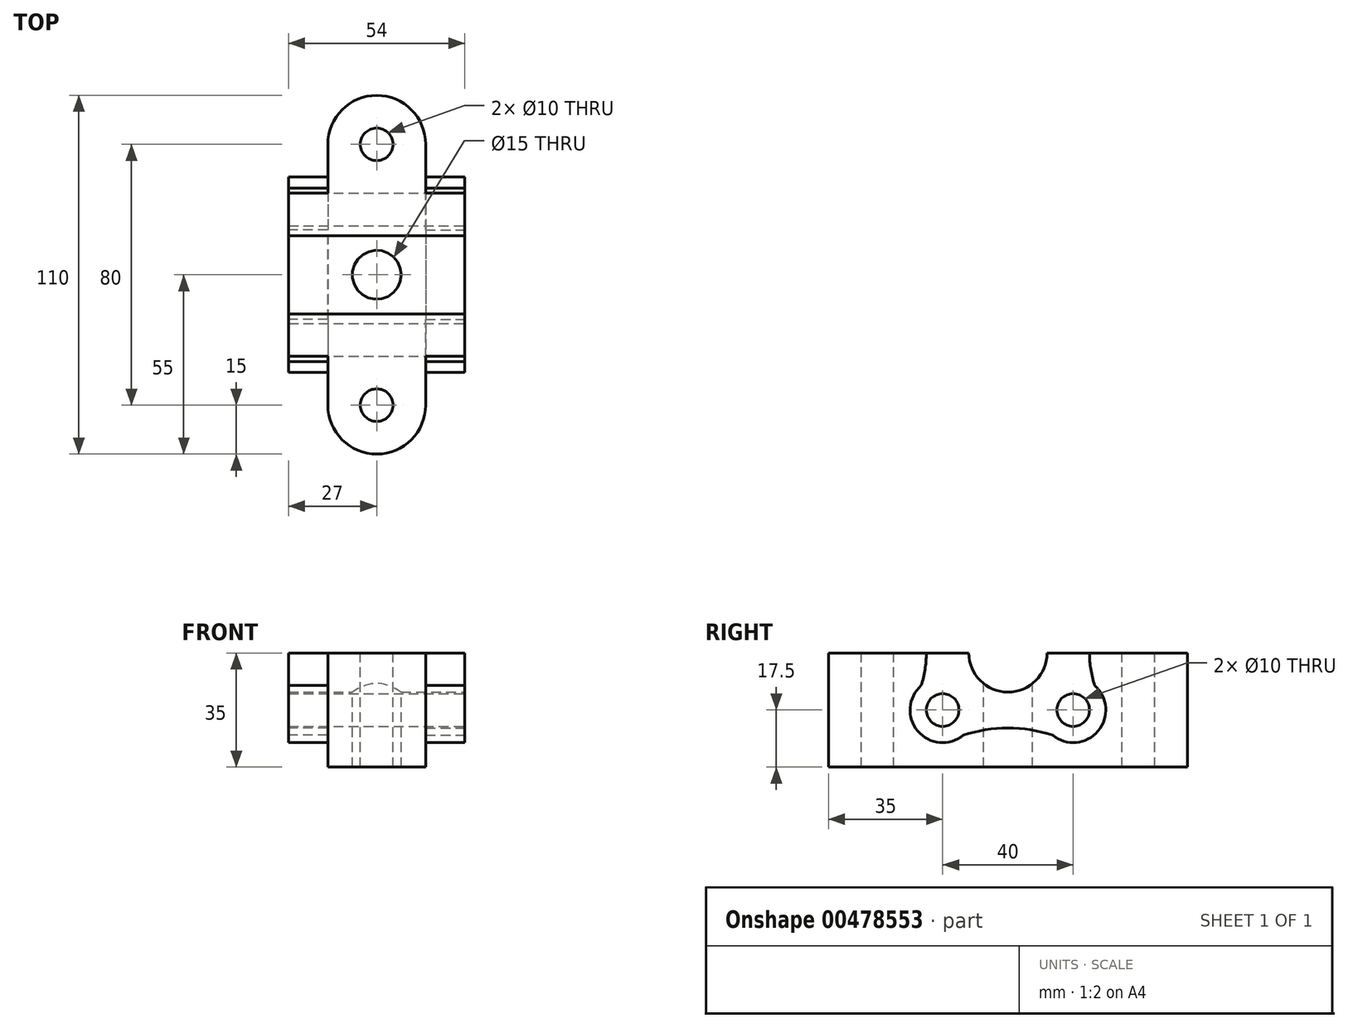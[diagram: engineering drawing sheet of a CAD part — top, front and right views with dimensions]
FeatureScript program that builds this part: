
annotation { "Feature Type Name" : "Feature", "Feature Type Description" : "" }
export const myFeature = defineFeature(function(context is Context, id is Id, definition is map)
    precondition{}
    {
        {
            var Q0;
            Q0=qCreatedBy(makeId("Top.planeOp"),FACE);
            var sketch = newSketch(context, id + "F0", { "sketchPlane" : qUnion([Q0])});
            skLineSegment(sketch, "E0.bottom", {"start": v(-25.95, 26.62) * mm, "end": v(28.05, 26.62) * mm});
            skLineSegment(sketch, "E0.top", {"start": v(-25.95, -53.38) * mm, "end": v(28.05, -53.38) * mm});
            skLineSegment(sketch, "E0.left", {"start": v(-25.95, 26.62) * mm, "end": v(-25.95, -53.38) * mm});
            skLineSegment(sketch, "E0.right", {"start": v(28.05, 26.62) * mm, "end": v(28.05, -53.38) * mm});
            skSolve(sketch);
        }
        {
            var Q0;
            Q0=makeQuery(id+"F0.imprint","IMPRINT",FACE,{"disambiguationData":[TD([[makeQuery(id+"F0.imprint","IMPRINT",EDGE,{"derivedFrom":sQuery(id+"F0.wireOp",EDGE,"E0.bottom")}),-1.0]])]});
            extrude(context, id + "F1", {"entities" : qUnion([Q0]), "depth" : 35 * mm});
        }
        {
            var Q0;
            Q0=makeQuery(id+"F1.opExtrude","SWEPT_FACE",FACE,{"disambiguationData":[OSD([sQuery(id+"F0.wireOp",EDGE,"E0.right")])]});
            var sketch = newSketch(context, id + "F2", { "sketchPlane" : qUnion([Q0])});
            skCircle(sketch, "E1", {"center": v(-13.38, 35) * mm, "radius": 12 * mm});
            skLineSegment(sketch, "E2", {"start": v(-25.38, 35) * mm, "end": v(-1.38, 35) * mm});
            skSolve(sketch);
        }
        {
            var Q0;
            Q0=makeQuery(id+"F1.opExtrude","CAP_FACE",FACE,{"disambiguationData":[OSD([sQuery(id+"F0.wireOp",EDGE,"E0.bottom"),sQuery(id+"F0.wireOp",EDGE,"E0.top"),sQuery(id+"F0.wireOp",EDGE,"E0.left"),sQuery(id+"F0.wireOp",EDGE,"E0.right")])],"isStart":false});
            var sketch = newSketch(context, id + "F3", { "sketchPlane" : qUnion([Q0])});
            skCircle(sketch, "E3", {"center": v(1.05, -13.38) * mm, "radius": 7.5 * mm});
            skSolve(sketch);
        }
        {
            var Q0;
            Q0=makeQuery(id+"F3.imprint","IMPRINT",FACE,{"disambiguationData":[TD([[makeQuery(id+"F3.imprint","IMPRINT",EDGE,{"derivedFrom":sQuery(id+"F3.wireOp",EDGE,"E3")}),1.0]])]});
            extrude(context, id + "F4", {"entities" : qUnion([Q0]), "operationType" : NewBodyOperationType.REMOVE, "oppositeDirection" : true, "depth" : 71.6 * mm});
        }
        {
            var Q0;
            {var subQ0=sQuery(id+"F2.wireOp",EDGE,"E2");Q0=makeQuery(id+"F2.imprint","IMPRINT",FACE,{"disambiguationData":[TD([[makeQuery(id+"F2.imprint","IMPRINT",EDGE,{"derivedFrom":subQ0}),1.0]])]});}
            extrude(context, id + "F5", {"entities" : qUnion([Q0]), "operationType" : NewBodyOperationType.REMOVE, "oppositeDirection" : true, "depth" : 80.1 * mm});
        }
        {
            var Q0;
            {var subQ0=sQuery(id+"F0.wireOp",EDGE,"E0.bottom");var subQ1=sQuery(id+"F0.wireOp",EDGE,"E0.right");var subQ2=sQuery(id+"F0.wireOp",EDGE,"E0.left");Q0=makeQuery(id+"F5.boolean.opBoolean","SPLIT",FACE,{"disambiguationData":[TD([makeQuery(id+"F1.opExtrude","SWEPT_FACE",FACE,{"disambiguationData":[OSD([subQ0])]})])],"derivedFrom":makeQuery(id+"F1.opExtrude","CAP_FACE",FACE,{"disambiguationData":[OSD([subQ0,sQuery(id+"F0.wireOp",EDGE,"E0.top"),subQ2,subQ1])],"isStart":false})});}
            var sketch = newSketch(context, id + "F6", { "sketchPlane" : qUnion([Q0])});
            skCircle(sketch, "E4", {"center": v(1.05, 26.62) * mm, "radius": 15 * mm});
            skLineSegment(sketch, "E5", {"start": v(1.05, 11.62) * mm, "end": v(28.05, 11.62) * mm});
            skPoint(sketch, "E5.endSnap0", {"position": v(28.05, 12.62) * mm});
            skLineSegment(sketch, "E6", {"start": v(1.05, 11.62) * mm, "end": v(-25.95, 11.62) * mm});
            skLineSegment(sketch, "E7", {"start": v(-13.95, 26.62) * mm, "end": v(-13.95, 11.62) * mm});
            skPoint(sketch, "E7.endSnap0", {"position": v(-12.45, 11.62) * mm});
            skLineSegment(sketch, "E8", {"start": v(16.05, 26.62) * mm, "end": v(16.05, 11.62) * mm});
            skCircle(sketch, "E9", {"center": v(1.05, 26.62) * mm, "radius": 5 * mm});
            skSolve(sketch);
        }
        {
            var Q0;
            {var subQ5=sQuery(id+"F6.wireOp",EDGE,"E7");Q0=makeQuery(id+"F6.imprint","IMPRINT",FACE,{"disambiguationData":[TD([[makeQuery(id+"F6.imprint","IMPRINT",EDGE,{"derivedFrom":subQ5}),-1.0]])]});}
            var Q1;
            {var subQ5=sQuery(id+"F6.wireOp",EDGE,"E8");Q1=makeQuery(id+"F6.imprint","IMPRINT",FACE,{"disambiguationData":[TD([[makeQuery(id+"F6.imprint","IMPRINT",EDGE,{"derivedFrom":subQ5}),1.0]])]});}
            extrude(context, id + "F7", {"entities" : qUnion([Q0, Q1]), "operationType" : NewBodyOperationType.REMOVE, "oppositeDirection" : true, "depth" : 52.7 * mm});
        }
        {
            var Q0;
            {var subQ1=makeQuery(id+"F1.opExtrude","CAP_EDGE",EDGE,{"disambiguationData":[OSD([sQuery(id+"F0.wireOp",EDGE,"E0.bottom")])],"isStart":false});var subQ4=sQuery(id+"F6.wireOp",EDGE,"E9");var subQ5=makeQuery(id+"F6.imprint","INTERSECT",VERTEX,{"disambiguationData":[OD(0.0)],"derivedFrom":[subQ1,subQ4]});Q0=makeQuery(id+"F6.imprint","IMPRINT",FACE,{"disambiguationData":[TD([[makeQuery(id+"F6.imprint","IMPRINT",EDGE,{"disambiguationData":[TD([[subQ5,1.0]])],"derivedFrom":subQ4}),-1.0]])]});}
            extrude(context, id + "F8", {"entities" : qUnion([Q0]), "operationType" : NewBodyOperationType.ADD, "oppositeDirection" : true, "depth" : 35 * mm});
        }
        {
            var Q0;
            {var subQ0=sQuery(id+"F6.wireOp",EDGE,"E9");var subQ1=makeQuery(id+"F1.opExtrude","CAP_EDGE",EDGE,{"disambiguationData":[OSD([sQuery(id+"F0.wireOp",EDGE,"E0.bottom")])],"isStart":false});var subQ2=makeQuery(id+"F6.imprint","INTERSECT",VERTEX,{"disambiguationData":[OD(0.0)],"derivedFrom":[subQ1,subQ0]});Q0=makeQuery(id+"F6.imprint","IMPRINT",FACE,{"disambiguationData":[TD([[makeQuery(id+"F6.imprint","IMPRINT",EDGE,{"disambiguationData":[TD([[subQ2,-1.0]])],"derivedFrom":subQ0}),1.0]])]});}
            extrude(context, id + "F9", {"entities" : qUnion([Q0]), "operationType" : NewBodyOperationType.REMOVE, "oppositeDirection" : true, "depth" : 60.9 * mm});
        }
        {
            var Q0;
            {var subQ0=sQuery(id+"F0.wireOp",EDGE,"E0.top");var subQ1=sQuery(id+"F0.wireOp",EDGE,"E0.left");var subQ2=sQuery(id+"F0.wireOp",EDGE,"E0.right");Q0=makeQuery(id+"F5.boolean.opBoolean","SPLIT",FACE,{"disambiguationData":[TD([makeQuery(id+"F1.opExtrude","SWEPT_FACE",FACE,{"disambiguationData":[OSD([subQ0])]})])],"derivedFrom":makeQuery(id+"F1.opExtrude","CAP_FACE",FACE,{"disambiguationData":[OSD([sQuery(id+"F0.wireOp",EDGE,"E0.bottom"),subQ0,subQ1,subQ2])],"isStart":false})});}
            var sketch = newSketch(context, id + "F10", { "sketchPlane" : qUnion([Q0])});
            skCircle(sketch, "E10", {"center": v(1.05, -53.38) * mm, "radius": 15 * mm});
            skLineSegment(sketch, "E11", {"start": v(1.05, -38.38) * mm, "end": v(28.05, -38.38) * mm});
            skLineSegment(sketch, "E12", {"start": v(1.05, -38.38) * mm, "end": v(-25.95, -38.38) * mm});
            skPoint(sketch, "E12.endSnap0", {"position": v(-25.95, -39.38) * mm});
            skLineSegment(sketch, "E13", {"start": v(16.05, -53.38) * mm, "end": v(16.05, -38.38) * mm});
            skLineSegment(sketch, "E14", {"start": v(-13.95, -53.38) * mm, "end": v(-13.95, -38.38) * mm});
            skCircle(sketch, "E15", {"center": v(1.05, -53.38) * mm, "radius": 5 * mm});
            skSolve(sketch);
        }
        {
            var Q0;
            {var subQ1=makeQuery(id+"F1.opExtrude","CAP_EDGE",EDGE,{"disambiguationData":[OSD([sQuery(id+"F0.wireOp",EDGE,"E0.top")])],"isStart":false});var subQ4=sQuery(id+"F10.wireOp",EDGE,"E15");var subQ5=makeQuery(id+"F10.imprint","INTERSECT",VERTEX,{"disambiguationData":[OD(0.0)],"derivedFrom":[subQ1,subQ4]});Q0=makeQuery(id+"F10.imprint","IMPRINT",FACE,{"disambiguationData":[TD([[makeQuery(id+"F10.imprint","IMPRINT",EDGE,{"disambiguationData":[TD([[subQ5,1.0]])],"derivedFrom":subQ4}),-1.0]])]});}
            extrude(context, id + "F11", {"entities" : qUnion([Q0]), "operationType" : NewBodyOperationType.ADD, "oppositeDirection" : true, "depth" : 35 * mm});
        }
        {
            var Q0;
            {var subQ0=sQuery(id+"F10.wireOp",EDGE,"E15");var subQ1=makeQuery(id+"F1.opExtrude","CAP_EDGE",EDGE,{"disambiguationData":[OSD([sQuery(id+"F0.wireOp",EDGE,"E0.top")])],"isStart":false});var subQ2=makeQuery(id+"F10.imprint","INTERSECT",VERTEX,{"disambiguationData":[OD(0.0)],"derivedFrom":[subQ1,subQ0]});Q0=makeQuery(id+"F10.imprint","IMPRINT",FACE,{"disambiguationData":[TD([[makeQuery(id+"F10.imprint","IMPRINT",EDGE,{"disambiguationData":[TD([[subQ2,-1.0]])],"derivedFrom":subQ0}),1.0]])]});}
            extrude(context, id + "F12", {"entities" : qUnion([Q0]), "operationType" : NewBodyOperationType.REMOVE, "oppositeDirection" : true, "depth" : 46.9 * mm});
        }
        {
            var Q0;
            {var subQ5=sQuery(id+"F10.wireOp",EDGE,"E14");Q0=makeQuery(id+"F10.imprint","IMPRINT",FACE,{"disambiguationData":[TD([[makeQuery(id+"F10.imprint","IMPRINT",EDGE,{"derivedFrom":subQ5}),1.0]])]});}
            var Q1;
            {var subQ5=sQuery(id+"F10.wireOp",EDGE,"E13");Q1=makeQuery(id+"F10.imprint","IMPRINT",FACE,{"disambiguationData":[TD([[makeQuery(id+"F10.imprint","IMPRINT",EDGE,{"derivedFrom":subQ5}),-1.0]])]});}
            extrude(context, id + "F13", {"entities" : qUnion([Q0, Q1]), "operationType" : NewBodyOperationType.REMOVE, "oppositeDirection" : true, "depth" : 46.9 * mm});
        }
        {
            var Q0;
            Q0=makeQuery(id+"F1.opExtrude","SWEPT_FACE",FACE,{"disambiguationData":[OSD([sQuery(id+"F0.wireOp",EDGE,"E0.left")])]});
            var sketch = newSketch(context, id + "F14", { "sketchPlane" : qUnion([Q0])});
            skCircle(sketch, "E16", {"center": v(-6.62, 17.5) * mm, "radius": 5 * mm});
            skCircle(sketch, "E17", {"center": v(33.38, 17.5) * mm, "radius": 5 * mm});
            skCircle(sketch, "E18", {"center": v(33.38, 17.5) * mm, "radius": 10 * mm});
            skCircle(sketch, "E19", {"center": v(-6.62, 17.5) * mm, "radius": 10 * mm});
            skArc(sketch, "E20", {"start": v(27.06, 9.75) * mm, "mid": v(13.38, 12) * mm, "end": v(-0.3, 9.75) * mm});
            skLineSegment(sketch, "E21", {"start": v(-6.62, 17.5) * mm, "end": v(-6.62, 35) * mm});
            skLineSegment(sketch, "E22", {"start": v(33.38, 17.5) * mm, "end": v(33.38, 35) * mm});
            skLineSegment(sketch, "E23", {"start": v(33.38, 17.5) * mm, "end": v(43.38, 17.5) * mm});
            skLineSegment(sketch, "E24", {"start": v(33.38, 22.5) * mm, "end": v(33.38, 27.5) * mm});
            skLineSegment(sketch, "E25", {"start": v(33.38, 25) * mm, "end": v(40, 25) * mm});
            skLineSegment(sketch, "E26", {"start": v(33.38, 35) * mm, "end": v(33.38, 27.5) * mm});
            skArc(sketch, "E27", {"start": v(38.38, 35) * mm, "mid": v(38.79, 29.94) * mm, "end": v(40, 25) * mm});
            skLineSegment(sketch, "E28", {"start": v(-6.62, 27.5) * mm, "end": v(-6.62, 22.5) * mm});
            skLineSegment(sketch, "E29", {"start": v(-6.62, 25) * mm, "end": v(-13.23, 25) * mm});
            skArc(sketch, "E30", {"start": v(-13.23, 25) * mm, "mid": v(-12.03, 29.94) * mm, "end": v(-11.62, 35) * mm});
            skSolve(sketch);
        }
        {
            var Q0;
            {var subQ0=sQuery(id+"F14.wireOp",EDGE,"E18");var subQ1=makeQuery(id+"F13.boolean.opBoolean","COPY",EDGE,{"derivedFrom":makeQuery(id+"F13.opExtrude","SWEPT_EDGE",EDGE,{"disambiguationData":[OSD([sQuery(id+"F0.wireOp",EDGE,"E0.left"),sQuery(id+"F10.wireOp",EDGE,"E12")])]})});var subQ2=makeQuery(id+"F14.imprint","INTERSECT",VERTEX,{"disambiguationData":[OD(0.0)],"derivedFrom":[subQ1,subQ0]});Q0=makeQuery(id+"F14.imprint","IMPRINT",FACE,{"disambiguationData":[TD([[makeQuery(id+"F14.imprint","IMPRINT",EDGE,{"disambiguationData":[TD([[subQ2,1.0]])],"derivedFrom":subQ0}),1.0]])]});}
            extrude(context, id + "F15", {"entities" : qUnion([Q0]), "operationType" : NewBodyOperationType.ADD, "oppositeDirection" : true, "depth" : 12 * mm});
        }
        {
            var Q0;
            {var subQ2=sQuery(id+"F14.wireOp",EDGE,"E20");Q0=makeQuery(id+"F14.imprint","IMPRINT",FACE,{"disambiguationData":[TD([[makeQuery(id+"F14.imprint","IMPRINT",EDGE,{"derivedFrom":subQ2}),1.0]])]});}
            extrude(context, id + "F16", {"entities" : qUnion([Q0]), "operationType" : NewBodyOperationType.REMOVE, "oppositeDirection" : true, "depth" : 12 * mm});
        }
        {
            var Q0;
            {var subQ0=sQuery(id+"F14.wireOp",EDGE,"E19");var subQ1=makeQuery(id+"F7.boolean.opBoolean","COPY",EDGE,{"derivedFrom":makeQuery(id+"F7.opExtrude","SWEPT_EDGE",EDGE,{"disambiguationData":[OSD([sQuery(id+"F0.wireOp",EDGE,"E0.left"),sQuery(id+"F6.wireOp",EDGE,"E6")])]})});var subQ2=makeQuery(id+"F14.imprint","INTERSECT",VERTEX,{"disambiguationData":[OD(0.0)],"derivedFrom":[subQ1,subQ0]});Q0=makeQuery(id+"F14.imprint","IMPRINT",FACE,{"disambiguationData":[TD([[makeQuery(id+"F14.imprint","IMPRINT",EDGE,{"disambiguationData":[TD([[subQ2,1.0]])],"derivedFrom":subQ0}),1.0]])]});}
            var Q1;
            {var subQ0=sQuery(id+"F14.wireOp",EDGE,"E30");Q1=makeQuery(id+"F14.imprint","IMPRINT",FACE,{"disambiguationData":[TD([[makeQuery(id+"F14.imprint","IMPRINT",EDGE,{"derivedFrom":subQ0}),-1.0]])]});}
            var Q2;
            {var subQ0=sQuery(id+"F14.wireOp",EDGE,"E29");var subQ1=sQuery(id+"F14.wireOp",EDGE,"E19");var subQ2=makeQuery(id+"F14.imprint","INTERSECT",VERTEX,{"derivedFrom":[subQ1,subQ0,sQuery(id+"F14.wireOp",EDGE,"E30")]});Q2=makeQuery(id+"F14.imprint","IMPRINT",FACE,{"disambiguationData":[TD([[makeQuery(id+"F14.imprint","IMPRINT",EDGE,{"disambiguationData":[TD([[subQ2,1.0]])],"derivedFrom":subQ1}),1.0]])]});}
            var Q3;
            {var subQ0=sQuery(id+"F14.wireOp",EDGE,"E27");Q3=makeQuery(id+"F14.imprint","IMPRINT",FACE,{"disambiguationData":[TD([[makeQuery(id+"F14.imprint","IMPRINT",EDGE,{"derivedFrom":subQ0}),-1.0]])]});}
            var Q4;
            {var subQ0=sQuery(id+"F14.wireOp",EDGE,"E25");var subQ1=sQuery(id+"F14.wireOp",EDGE,"E18");var subQ2=makeQuery(id+"F14.imprint","INTERSECT",VERTEX,{"derivedFrom":[subQ1,subQ0,sQuery(id+"F14.wireOp",EDGE,"E27")]});Q4=makeQuery(id+"F14.imprint","IMPRINT",FACE,{"disambiguationData":[TD([[makeQuery(id+"F14.imprint","IMPRINT",EDGE,{"disambiguationData":[TD([[subQ2,-1.0]])],"derivedFrom":subQ1}),1.0]])]});}
            var Q5;
            {var subQ0=sQuery(id+"F14.wireOp",EDGE,"E23");var subQ1=sQuery(id+"F14.wireOp",EDGE,"E18");var subQ2=makeQuery(id+"F14.imprint","INTERSECT",VERTEX,{"derivedFrom":[subQ1,subQ0]});Q5=makeQuery(id+"F14.imprint","IMPRINT",FACE,{"disambiguationData":[TD([[makeQuery(id+"F14.imprint","IMPRINT",EDGE,{"disambiguationData":[TD([[subQ2,-1.0]])],"derivedFrom":subQ1}),1.0]])]});}
            var Q6;
            {var subQ0=sQuery(id+"F14.wireOp",EDGE,"E23");var subQ1=sQuery(id+"F14.wireOp",EDGE,"E18");var subQ2=makeQuery(id+"F14.imprint","INTERSECT",VERTEX,{"derivedFrom":[subQ1,subQ0]});Q6=makeQuery(id+"F14.imprint","IMPRINT",FACE,{"disambiguationData":[TD([[makeQuery(id+"F14.imprint","IMPRINT",EDGE,{"disambiguationData":[TD([[subQ2,1.0]])],"derivedFrom":subQ1}),1.0]])]});}
            extrude(context, id + "F17", {"entities" : qUnion([Q0, Q1, Q2, Q3, Q4, Q5, Q6]), "operationType" : NewBodyOperationType.ADD, "oppositeDirection" : true, "depth" : 12 * mm});
        }
        {
            var Q0;
            Q0=makeQuery(id+"F1.opExtrude","SWEPT_FACE",FACE,{"disambiguationData":[OSD([sQuery(id+"F0.wireOp",EDGE,"E0.right")])]});
            var sketch = newSketch(context, id + "F18", { "sketchPlane" : qUnion([Q0])});
            skCircle(sketch, "E31", {"center": v(-33.38, 17.5) * mm, "radius": 5 * mm});
            skCircle(sketch, "E32", {"center": v(-33.38, 17.5) * mm, "radius": 10 * mm});
            skPoint(sketch, "E33.endSnap0", {"position": v(11.62, 17.5) * mm});
            skCircle(sketch, "E34", {"center": v(6.62, 17.5) * mm, "radius": 5 * mm});
            skCircle(sketch, "E35", {"center": v(6.62, 17.5) * mm, "radius": 10 * mm});
            skLineSegment(sketch, "E36", {"start": v(6.62, 12) * mm, "end": v(6.62, 7.5) * mm});
            skLineSegment(sketch, "E37", {"start": v(-33.38, 12) * mm, "end": v(-33.38, 7.5) * mm});
            skArc(sketch, "E38", {"start": v(0.3, 9.75) * mm, "mid": v(-13.38, 12) * mm, "end": v(-27.06, 9.75) * mm});
            skLineSegment(sketch, "E39", {"start": v(6.62, 27.5) * mm, "end": v(6.62, 22.5) * mm});
            skLineSegment(sketch, "E40", {"start": v(6.62, 25) * mm, "end": v(13.23, 25) * mm});
            skArc(sketch, "E41", {"start": v(11.62, 35) * mm, "mid": v(12.03, 29.94) * mm, "end": v(13.23, 25) * mm});
            skLineSegment(sketch, "E42", {"start": v(-33.38, 27.5) * mm, "end": v(-33.38, 22.5) * mm});
            skLineSegment(sketch, "E43", {"start": v(-33.38, 25) * mm, "end": v(-40, 25) * mm});
            skArc(sketch, "E44", {"start": v(-40, 25) * mm, "mid": v(-38.79, 29.94) * mm, "end": v(-38.38, 35) * mm});
            skSolve(sketch);
        }
        {
            var Q0;
            {var subQ0=sQuery(id+"F18.wireOp",EDGE,"E43");var subQ1=sQuery(id+"F18.wireOp",EDGE,"E32");var subQ2=makeQuery(id+"F18.imprint","INTERSECT",VERTEX,{"derivedFrom":[subQ1,subQ0,sQuery(id+"F18.wireOp",EDGE,"E44")]});Q0=makeQuery(id+"F18.imprint","IMPRINT",FACE,{"disambiguationData":[TD([[makeQuery(id+"F18.imprint","IMPRINT",EDGE,{"disambiguationData":[TD([[subQ2,-1.0]])],"derivedFrom":subQ1}),1.0]])]});}
            var Q1;
            {var subQ0=sQuery(id+"F18.wireOp",EDGE,"E40");var subQ1=sQuery(id+"F18.wireOp",EDGE,"E35");var subQ2=makeQuery(id+"F18.imprint","INTERSECT",VERTEX,{"derivedFrom":[subQ1,subQ0,sQuery(id+"F18.wireOp",EDGE,"E41")]});Q1=makeQuery(id+"F18.imprint","IMPRINT",FACE,{"disambiguationData":[TD([[makeQuery(id+"F18.imprint","IMPRINT",EDGE,{"disambiguationData":[TD([[subQ2,1.0]])],"derivedFrom":subQ1}),1.0]])]});}
            extrude(context, id + "F19", {"entities" : qUnion([Q0, Q1]), "operationType" : NewBodyOperationType.ADD, "oppositeDirection" : true, "depth" : 12 * mm});
        }
        {
            var Q0;
            {var subQ5=sQuery(id+"F18.wireOp",EDGE,"E38");Q0=makeQuery(id+"F18.imprint","IMPRINT",FACE,{"disambiguationData":[TD([[makeQuery(id+"F18.imprint","IMPRINT",EDGE,{"derivedFrom":subQ5}),1.0]])]});}
            extrude(context, id + "F20", {"entities" : qUnion([Q0]), "operationType" : NewBodyOperationType.REMOVE, "oppositeDirection" : true, "depth" : 12 * mm});
        }
        {
            var Q0;
            {var subQ0=sQuery(id+"F18.wireOp",EDGE,"E44");Q0=makeQuery(id+"F18.imprint","IMPRINT",FACE,{"disambiguationData":[TD([[makeQuery(id+"F18.imprint","IMPRINT",EDGE,{"derivedFrom":subQ0}),-1.0]])]});}
            var Q1;
            {var subQ0=sQuery(id+"F18.wireOp",EDGE,"E43");var subQ1=sQuery(id+"F18.wireOp",EDGE,"E32");var subQ2=makeQuery(id+"F18.imprint","INTERSECT",VERTEX,{"derivedFrom":[subQ1,subQ0,sQuery(id+"F18.wireOp",EDGE,"E44")]});Q1=makeQuery(id+"F18.imprint","IMPRINT",FACE,{"disambiguationData":[TD([[makeQuery(id+"F18.imprint","IMPRINT",EDGE,{"disambiguationData":[TD([[subQ2,1.0]])],"derivedFrom":subQ1}),1.0]])]});}
            var Q2;
            {var subQ0=sQuery(id+"F18.wireOp",EDGE,"E41");Q2=makeQuery(id+"F18.imprint","IMPRINT",FACE,{"disambiguationData":[TD([[makeQuery(id+"F18.imprint","IMPRINT",EDGE,{"derivedFrom":subQ0}),-1.0]])]});}
            var Q3;
            {var subQ0=sQuery(id+"F18.wireOp",EDGE,"E40");var subQ1=sQuery(id+"F18.wireOp",EDGE,"E35");var subQ2=makeQuery(id+"F18.imprint","INTERSECT",VERTEX,{"derivedFrom":[subQ1,subQ0,sQuery(id+"F18.wireOp",EDGE,"E41")]});Q3=makeQuery(id+"F18.imprint","IMPRINT",FACE,{"disambiguationData":[TD([[makeQuery(id+"F18.imprint","IMPRINT",EDGE,{"disambiguationData":[TD([[subQ2,-1.0]])],"derivedFrom":subQ1}),1.0]])]});}
            extrude(context, id + "F21", {"entities" : qUnion([Q0, Q1, Q2, Q3]), "operationType" : NewBodyOperationType.ADD, "oppositeDirection" : true, "depth" : 12 * mm});
        }
        {
            var Q0;
            {var subQ0=sQuery(id+"F18.wireOp",EDGE,"E31");var subQ1=makeQuery(id+"F18.imprint","INTERSECT",VERTEX,{"derivedFrom":[subQ0,sQuery(id+"F18.wireOp",EDGE,"E42")]});Q0=makeQuery(id+"F18.imprint","IMPRINT",FACE,{"disambiguationData":[TD([[makeQuery(id+"F18.imprint","IMPRINT",EDGE,{"disambiguationData":[TD([[subQ1,-1.0]])],"derivedFrom":subQ0}),1.0]])]});}
            var Q1;
            {var subQ0=sQuery(id+"F18.wireOp",EDGE,"E34");var subQ1=makeQuery(id+"F18.imprint","INTERSECT",VERTEX,{"derivedFrom":[subQ0,sQuery(id+"F18.wireOp",EDGE,"E39")]});Q1=makeQuery(id+"F18.imprint","IMPRINT",FACE,{"disambiguationData":[TD([[makeQuery(id+"F18.imprint","IMPRINT",EDGE,{"disambiguationData":[TD([[subQ1,1.0]])],"derivedFrom":subQ0}),1.0]])]});}
            extrude(context, id + "F22", {"entities" : qUnion([Q0, Q1]), "operationType" : NewBodyOperationType.REMOVE, "oppositeDirection" : true, "depth" : 72.1 * mm});
        }
    });
